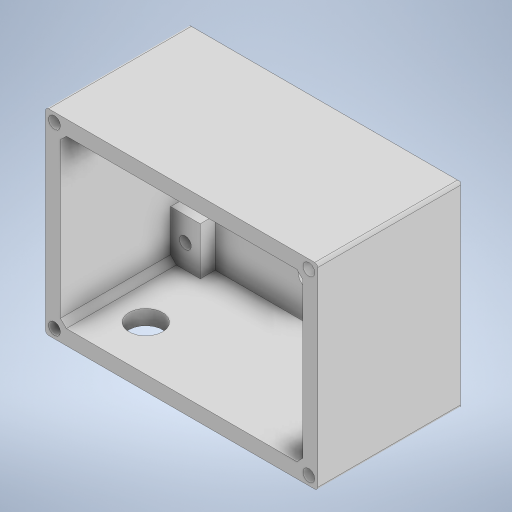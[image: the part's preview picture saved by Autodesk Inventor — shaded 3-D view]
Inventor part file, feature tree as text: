
AUTODESK INVENTOR PART (.ipt)
format: ipt  version: 2024 (Build 280153000, 153)  size: 339,456 bytes
history: native  units: in
note: dims shown in document units (in); Inventor stores cm internally (conversion verified against a paired STEP export)
features: sketch x9, hole x5, extrude x4, chamfer x2, fillet x1
ambient origin geometry x8: Origin, YZ Plane, XZ Plane, XY Plane, X Axis, Y Axis, Z Axis, Center Point
bodies: Solid1 (feature_tree)
feature tree (21):
  extrude  "Extrusion1"  Depth=3.6024in
  extrude  "Extrusion2"  Depth=0.1969in
  hole  "Hole1"  [1 undecoded]
  hole  "Hole3"  [1 undecoded]
  extrude  "Extrusion3"  Depth=0.315in
  hole  "Hole4"  [1 undecoded]
  hole  "Hole5"  [1 undecoded]
  extrude  "Extrusion4"  Depth=0.0394in
  hole  "Hole6"  [1 undecoded]
  chamfer  "Chamfer1"  Distance=0.0394in
  fillet  "Fillet2"  Radius=0.0394in
  chamfer  "Chamfer2"  [1 undecoded]
  sketch  "Sketch1"  dims[d1=2.5984in d2=3.6024in]
  sketch  "Sketch2"  dims[d3=1.9685in d4=0.0in d5=0.1969in]
  sketch  "Sketch3"  dims[d6=0.1969in d7=0.1969in]
  sketch  "Sketch5"  dims[d8=0.1969in d9=1.6535in d10=0.0in]
  sketch  "Sketch6"  dims[d11=1.1811in]
  sketch  "Sketch7"  dims[d12=0.2205in d13=0.2362in d14=0.1575in d15=0.0787in d16=90.0deg d17=0.315in d18=0.8108in d26=0.8in]
  sketch  "Sketch8"  dims[d27=0.8in]
  sketch  "Sketch9"  dims[d28=0.1575in d29=0.2362in d30=0.1575in d31=0.0787in d32=90.0deg d33=0.315in d34=0.8108in d35=0.0394in]
  sketch  "Sketch10"  dims[d36=0.0394in d37=0.0394in d38=0.0394in d39=0.0394in d40=0.0394in d41=0.0394in d42=0.0in d43=0.0in d44=0.1181in d45=0.1181in d46=0.1575in d47=0.2362in d48=0.1575in d49=0.0787in d50=90.0deg d51=0.3937in d52=0.8108in d53=0.4449in d54=0.2362in d55=0.1575in d56=0.0787in d57=90.0deg d58=0.3937in d59=0.8108in d60=0.1575in d61=0.2362in d62=0.1575in d63=0.0787in d64=90.0deg d65=0.3937in d66=0.8108in d67=0.315in d68=0.315in d69=2.815in d70=0.1969in d71=0.3937in d72=0.3937in d73=0.1969in d74=0.0in d75=2.874in d76=1.3701in d78=0.0787in d79=0.0787in d80=45.0deg d81=0.0394in d82=0.0394in d83=0.0787in d84=45.0deg d85=0.6299in d86=0.6299in]
note: 6 required parameter values undecoded (feature->parameter linkage not recoverable at this tier; creation-order binding heuristic only, values carry confidence <= 0.55)
